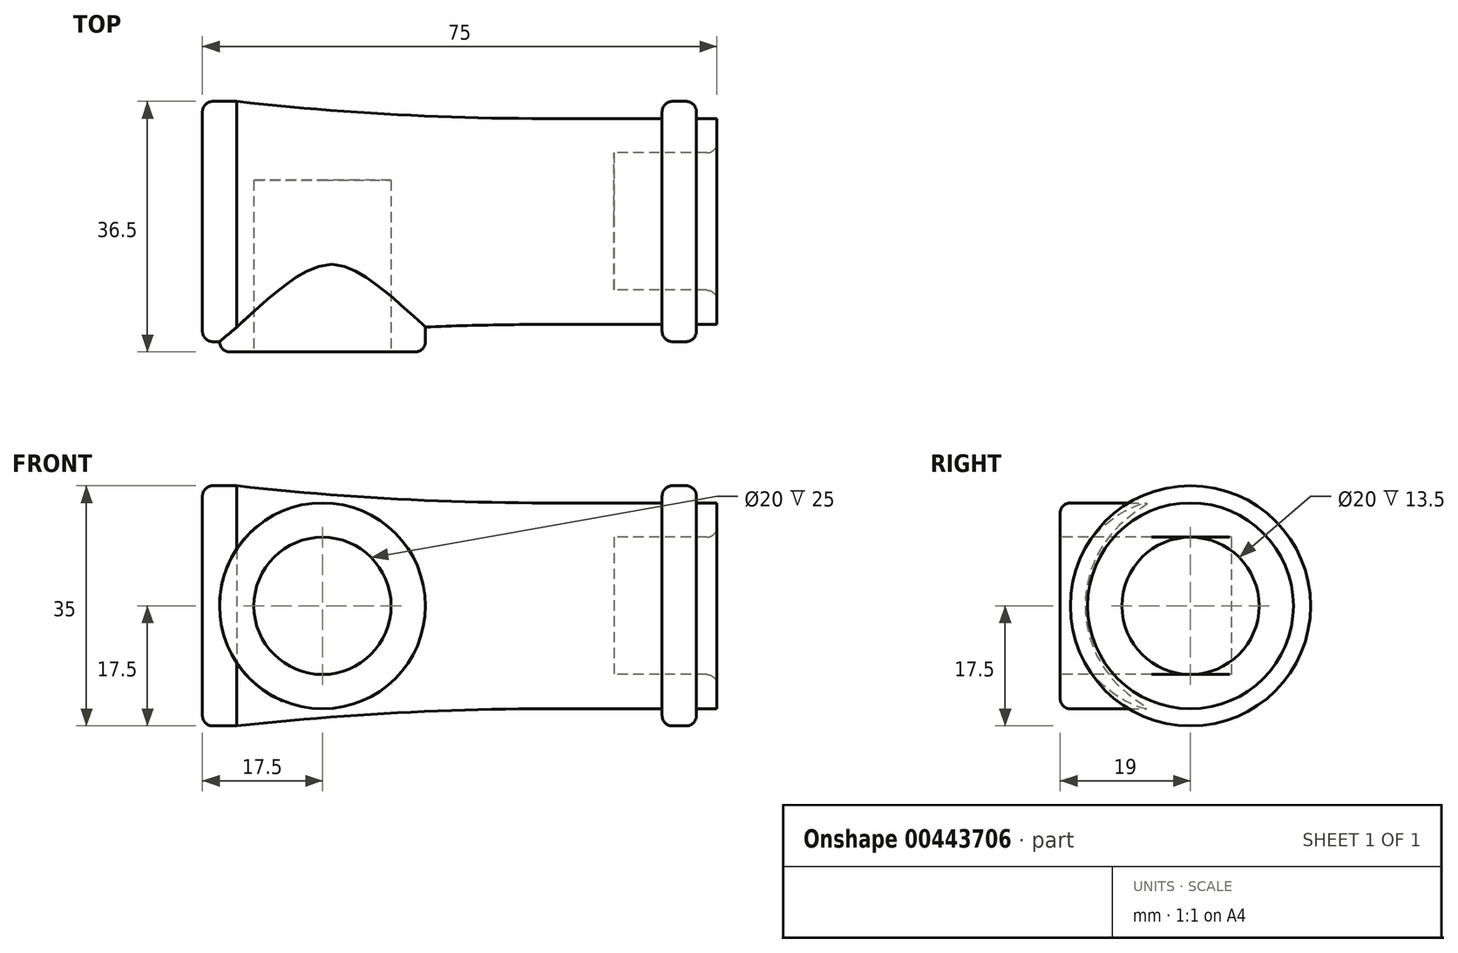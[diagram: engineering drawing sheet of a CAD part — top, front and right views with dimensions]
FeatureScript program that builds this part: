
annotation { "Feature Type Name" : "Feature", "Feature Type Description" : "" }
export const myFeature = defineFeature(function(context is Context, id is Id, definition is map)
    precondition{}
    {
        {
            var Q0;
            Q0=qCreatedBy(makeId("Front.planeOp"),FACE);
            var sketch = newSketch(context, id + "F0", { "sketchPlane" : qUnion([Q0])});
            skLineSegment(sketch, "E0", {"start": v(0, 0) * mm, "end": v(0, 17.5) * mm});
            skLineSegment(sketch, "E1", {"start": v(0, 17.5) * mm, "end": v(5, 17.5) * mm});
            skLineSegment(sketch, "E2", {"start": v(0, 0) * mm, "end": v(60, 0) * mm});
            skLineSegment(sketch, "E3", {"start": v(60, 0) * mm, "end": v(60, 10) * mm});
            skLineSegment(sketch, "E4", {"start": v(60, 10) * mm, "end": v(75, 10) * mm});
            skLineSegment(sketch, "E5", {"start": v(75, 10) * mm, "end": v(75, 15) * mm});
            skLineSegment(sketch, "E6", {"start": v(75, 15) * mm, "end": v(72, 15) * mm});
            skLineSegment(sketch, "E7", {"start": v(72, 15) * mm, "end": v(72, 17.5) * mm});
            skLineSegment(sketch, "E8", {"start": v(72, 17.5) * mm, "end": v(67, 17.5) * mm});
            skLineSegment(sketch, "E9", {"start": v(67, 17.5) * mm, "end": v(67, 15) * mm});
            skLineSegment(sketch, "E10", {"start": v(67, 15) * mm, "end": v(50, 15) * mm});
            skArc(sketch, "E11", {"start": v(5, 17.5) * mm, "mid": v(27.47, 15.63) * mm, "end": v(50, 15) * mm});
            skSolve(sketch);
        }
        {
            var Q0;
            Q0 = qSketchRegion(id + "F0", true);
            var Q1;
            Q1=sQuery(id+"F0.wireOp",EDGE,"E2");
            revolve(context, id + "F1", {"entities" : qUnion([Q0]), "axis" : qUnion([Q1]), "revolveType" : RevolveType.FULL});
        }
        {
            var Q0;
            Q0=qCreatedBy(makeId("Front.planeOp"),FACE);
            var sketch = newSketch(context, id + "F2", { "sketchPlane" : qUnion([Q0])});
            skCircle(sketch, "E12", {"center": v(17.5, 0) * mm, "radius": 15 * mm});
            skSolve(sketch);
        }
        {
            var Q0;
            Q0 = qSketchRegion(id + "F2", true);
            extrude(context, id + "F3", {"entities" : qUnion([Q0]), "operationType" : NewBodyOperationType.ADD, "depth" : 19 * mm});
        }
        {
            var Q0;
            Q0=makeQuery(id+"F3.opExtrude","CAP_FACE",FACE,{"disambiguationData":[OSD([sQuery(id+"F2.wireOp",EDGE,"E12")])],"isStart":false});
            var sketch = newSketch(context, id + "F4", { "sketchPlane" : qUnion([Q0])});
            skCircle(sketch, "E13", {"center": v(17.5, 0) * mm, "radius": 10 * mm});
            skSolve(sketch);
        }
        {
            var Q0;
            Q0 = qSketchRegion(id + "F4", true);
            extrude(context, id + "F5", {"entities" : qUnion([Q0]), "operationType" : NewBodyOperationType.REMOVE, "oppositeDirection" : true, "depth" : 25 * mm});
        }
        {
            var Q0;
            Q0=makeQuery(id+"F1.opRevolve","SWEPT_EDGE",EDGE,{"disambiguationData":[OSD([sQuery(id+"F0.wireOp",EDGE,"E0"),sQuery(id+"F0.wireOp",EDGE,"E1")])]});
            var Q1;
            Q1=makeQuery(id+"F3.opExtrude","CAP_EDGE",EDGE,{"disambiguationData":[OSD([sQuery(id+"F2.wireOp",EDGE,"E12")])],"isStart":false});
            var Q2;
            Q2=makeQuery(id+"F1.opRevolve","SWEPT_EDGE",EDGE,{"disambiguationData":[OSD([sQuery(id+"F0.wireOp",EDGE,"E8"),sQuery(id+"F0.wireOp",EDGE,"E9")])]});
            var Q3;
            Q3=makeQuery(id+"F1.opRevolve","SWEPT_EDGE",EDGE,{"disambiguationData":[OSD([sQuery(id+"F0.wireOp",EDGE,"E7"),sQuery(id+"F0.wireOp",EDGE,"E8")])]});
            var Q4;
            Q4=makeQuery(id+"F1.opRevolve","SWEPT_EDGE",EDGE,{"disambiguationData":[OSD([sQuery(id+"F0.wireOp",EDGE,"E4"),sQuery(id+"F0.wireOp",EDGE,"E5")])]});
            fillet(context, id + "F6", {"entities" : qUnion([Q0, Q1, Q2, Q3, Q4]), "radius" : 1.5 * mm, "tangentPropagation" : true, "allowEdgeOverflow" : false});
        }
    });
